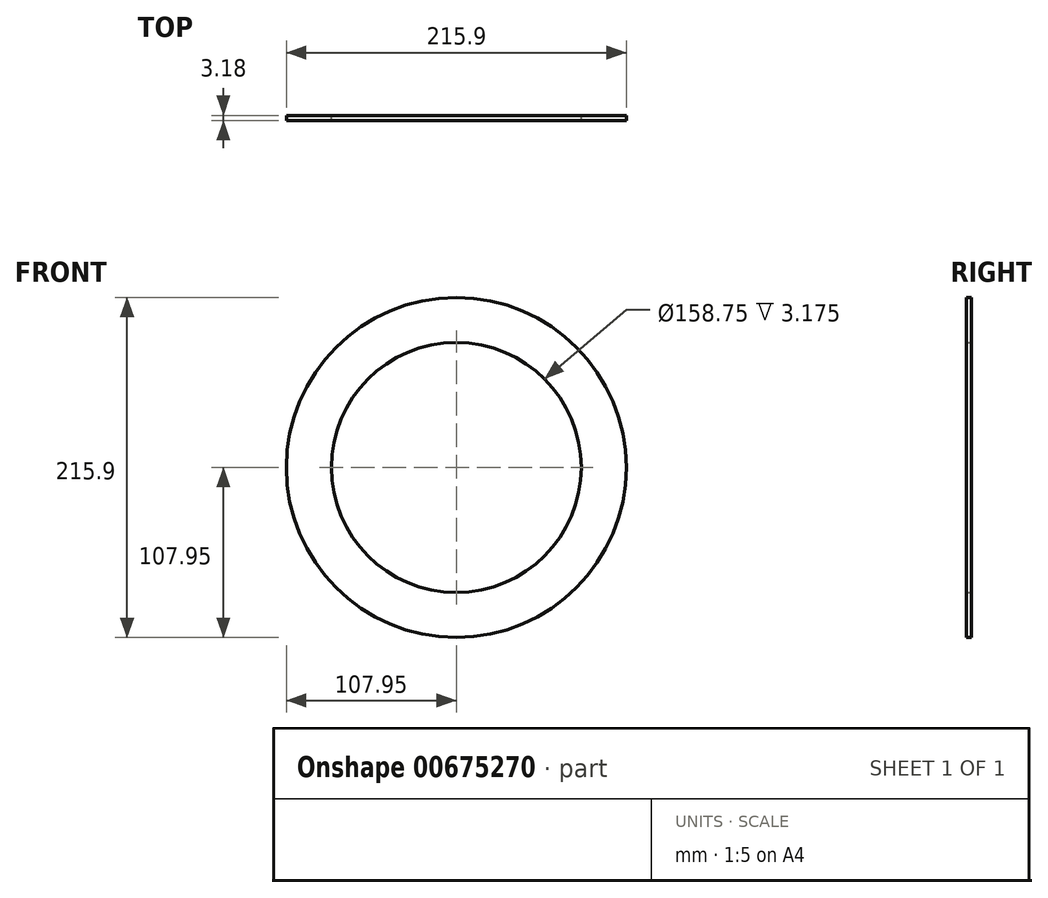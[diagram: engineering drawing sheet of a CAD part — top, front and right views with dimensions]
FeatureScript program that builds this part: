
annotation { "Feature Type Name" : "Feature", "Feature Type Description" : "" }
export const myFeature = defineFeature(function(context is Context, id is Id, definition is map)
    precondition{}
    {
        {
            var Q0;
            Q0=qCreatedBy(makeId("Front.planeOp"),FACE);
            var sketch = newSketch(context, id + "F0", { "sketchPlane" : qUnion([Q0])});
            skCircle(sketch, "E0", {"center": v(0, 0) * mm, "radius": 79.38 * mm});
            skCircle(sketch, "E1", {"center": v(0, 0) * mm, "radius": 107.95 * mm});
            skSolve(sketch);
        }
        {
            var Q0;
            Q0 = qSketchRegion(id + "F0", true);
            extrude(context, id + "F1", {"entities" : qUnion([Q0]), "depth" : 3.17 * mm, "offsetDistance" : 25.4 * mm});
        }
    });
